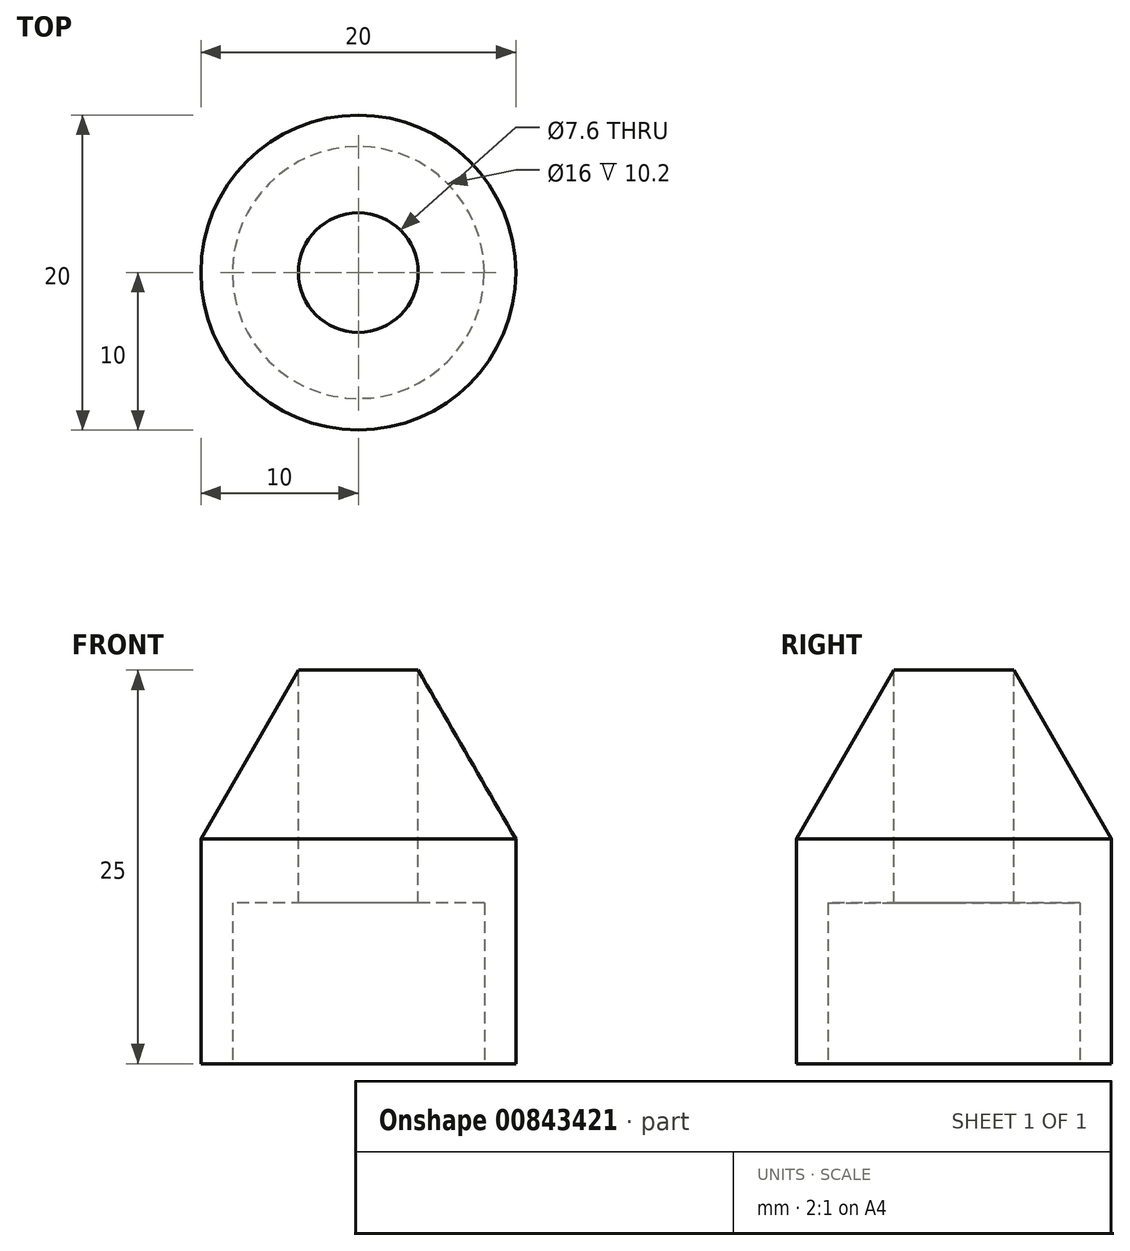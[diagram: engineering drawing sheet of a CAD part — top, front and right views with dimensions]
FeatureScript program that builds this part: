
annotation { "Feature Type Name" : "Feature", "Feature Type Description" : "" }
export const myFeature = defineFeature(function(context is Context, id is Id, definition is map)
    precondition{}
    {
        {
            var Q0;
            Q0=qCreatedBy(makeId("Top.planeOp"),FACE);
            var sketch = newSketch(context, id + "F0", { "sketchPlane" : qUnion([Q0])});
            skCircle(sketch, "E0", {"center": v(0, 0) * mm, "radius": 10 * mm});
            skSolve(sketch);
        }
        {
            var Q0;
            Q0=makeQuery(id+"F0.imprint","IMPRINT",FACE,{"disambiguationData":[TD([[makeQuery(id+"F0.imprint","IMPRINT",EDGE,{"derivedFrom":sQuery(id+"F0.wireOp",EDGE,"E0")}),1.0]])]});
            extrude(context, id + "F1", {"entities" : qUnion([Q0]), "depth" : 25 * mm, "offsetDistance" : 25 * mm});
        }
        {
            var Q0;
            Q0=makeQuery(id+"F1.opExtrude","CAP_FACE",FACE,{"disambiguationData":[OSD([sQuery(id+"F0.wireOp",EDGE,"E0")])],"isStart":false});
            chamfer(context, id + "F2", {"entities" : qUnion([Q0]), "chamferType" : ChamferType.OFFSET_ANGLE, "width" : 6.2 * mm, "oppositeDirection" : false, "angle" : 60 * degree, "tangentPropagation" : true});
        }
        {
            var Q0;
            Q0=makeQuery(id+"F1.opExtrude","CAP_FACE",FACE,{"disambiguationData":[OSD([sQuery(id+"F0.wireOp",EDGE,"E0")])],"isStart":false});
            var sketch = newSketch(context, id + "F3", { "sketchPlane" : qUnion([Q0])});
            skPoint(sketch, "E1", {"position": v(0, 3.8) * mm});
            skPoint(sketch, "E2", {"position": v(0, -3.8) * mm});
            skSolve(sketch);
        }
        {
            var Q0;
            {var subQ0=sQuery(id+"F0.wireOp",EDGE,"E0");Q0=makeQuery(id+"F3.imprint","IMPRINT",FACE,{"disambiguationData":[TD([[makeQuery(id+"F3.imprint","IMPRINT",EDGE,{"derivedFrom":makeQuery(id+"F2.opChamfer","BLEND_EDGE",EDGE,{"blendedFrom":[makeQuery(id+"F1.opExtrude","CAP_EDGE",EDGE,{"disambiguationData":[OSD([subQ0])],"isStart":false}),makeQuery(id+"F1.opExtrude","CAP_FACE",FACE,{"disambiguationData":[OSD([subQ0])],"isStart":false})],"blendedInto":[makeQuery(id+"F1.opExtrude","CAP_FACE",FACE,{"disambiguationData":[OSD([subQ0])],"isStart":false})]})}),1.0]])]});}
            extrude(context, id + "F4", {"entities" : qUnion([Q0]), "operationType" : NewBodyOperationType.REMOVE, "oppositeDirection" : true, "depth" : 40.7 * mm, "offsetDistance" : 25 * mm});
        }
        {
            var Q0;
            Q0=qCreatedBy(makeId("Top.planeOp"),FACE);
            var sketch = newSketch(context, id + "F5", { "sketchPlane" : qUnion([Q0])});
            skCircle(sketch, "E3", {"center": v(0, 0) * mm, "radius": 8 * mm});
            skSolve(sketch);
        }
        {
            var Q0;
            Q0=makeQuery(id+"F5.imprint","IMPRINT",FACE,{"disambiguationData":[TD([[makeQuery(id+"F5.imprint","IMPRINT",EDGE,{"derivedFrom":sQuery(id+"F5.wireOp",EDGE,"E3")}),1.0]])]});
            extrude(context, id + "F6", {"entities" : qUnion([Q0]), "operationType" : NewBodyOperationType.REMOVE, "depth" : 10.2 * mm, "offsetDistance" : 25 * mm});
        }
    });
